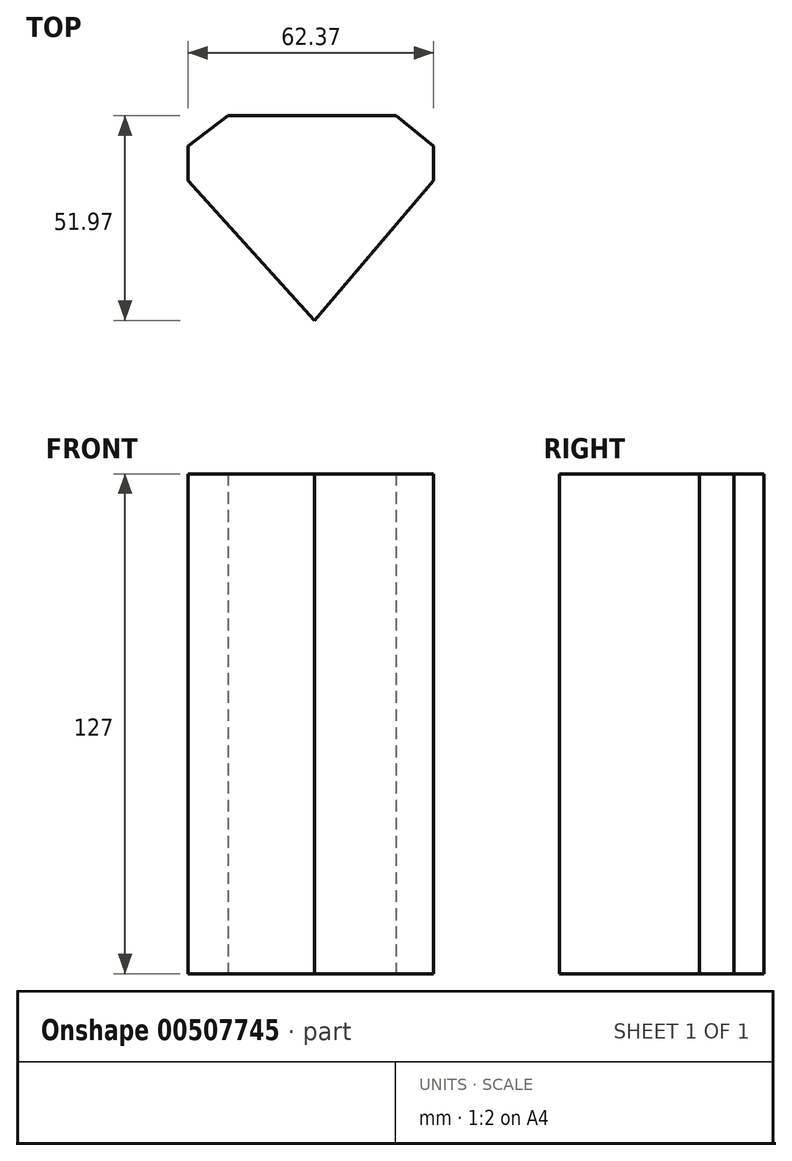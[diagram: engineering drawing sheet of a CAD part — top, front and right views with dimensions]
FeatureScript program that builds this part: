
annotation { "Feature Type Name" : "Feature", "Feature Type Description" : "" }
export const myFeature = defineFeature(function(context is Context, id is Id, definition is map)
    precondition{}
    {
        {
            var Q0;
            Q0=qCreatedBy(makeId("Top.planeOp"),FACE);
            var sketch = newSketch(context, id + "F0", { "sketchPlane" : qUnion([Q0])});
            skLineSegment(sketch, "E0", {"start": v(-32.18, 0) * mm, "end": v(-32.18, 8.74) * mm});
            skLineSegment(sketch, "E1", {"start": v(-32.18, 8.74) * mm, "end": v(-22.06, 16.4) * mm});
            skLineSegment(sketch, "E2", {"start": v(-22.06, 16.4) * mm, "end": v(20.61, 16.4) * mm});
            skLineSegment(sketch, "E3", {"start": v(20.61, 16.4) * mm, "end": v(30.19, 8.74) * mm});
            skLineSegment(sketch, "E4", {"start": v(30.19, 8.74) * mm, "end": v(30.19, 0) * mm});
            skLineSegment(sketch, "E5", {"start": v(-32.18, 0) * mm, "end": v(0, -35.57) * mm});
            skLineSegment(sketch, "E6", {"start": v(30.19, 0) * mm, "end": v(0, -35.57) * mm});
            skSolve(sketch);
        }
        {
            var Q0;
            Q0=makeQuery(id+"F0.imprint","IMPRINT",FACE,{"disambiguationData":[TD([[makeQuery(id+"F0.imprint","IMPRINT",EDGE,{"derivedFrom":sQuery(id+"F0.wireOp",EDGE,"E0")}),-1.0]])]});
            extrude(context, id + "F1", {"entities" : qUnion([Q0]), "depth" : 127 * mm});
        }
    });
